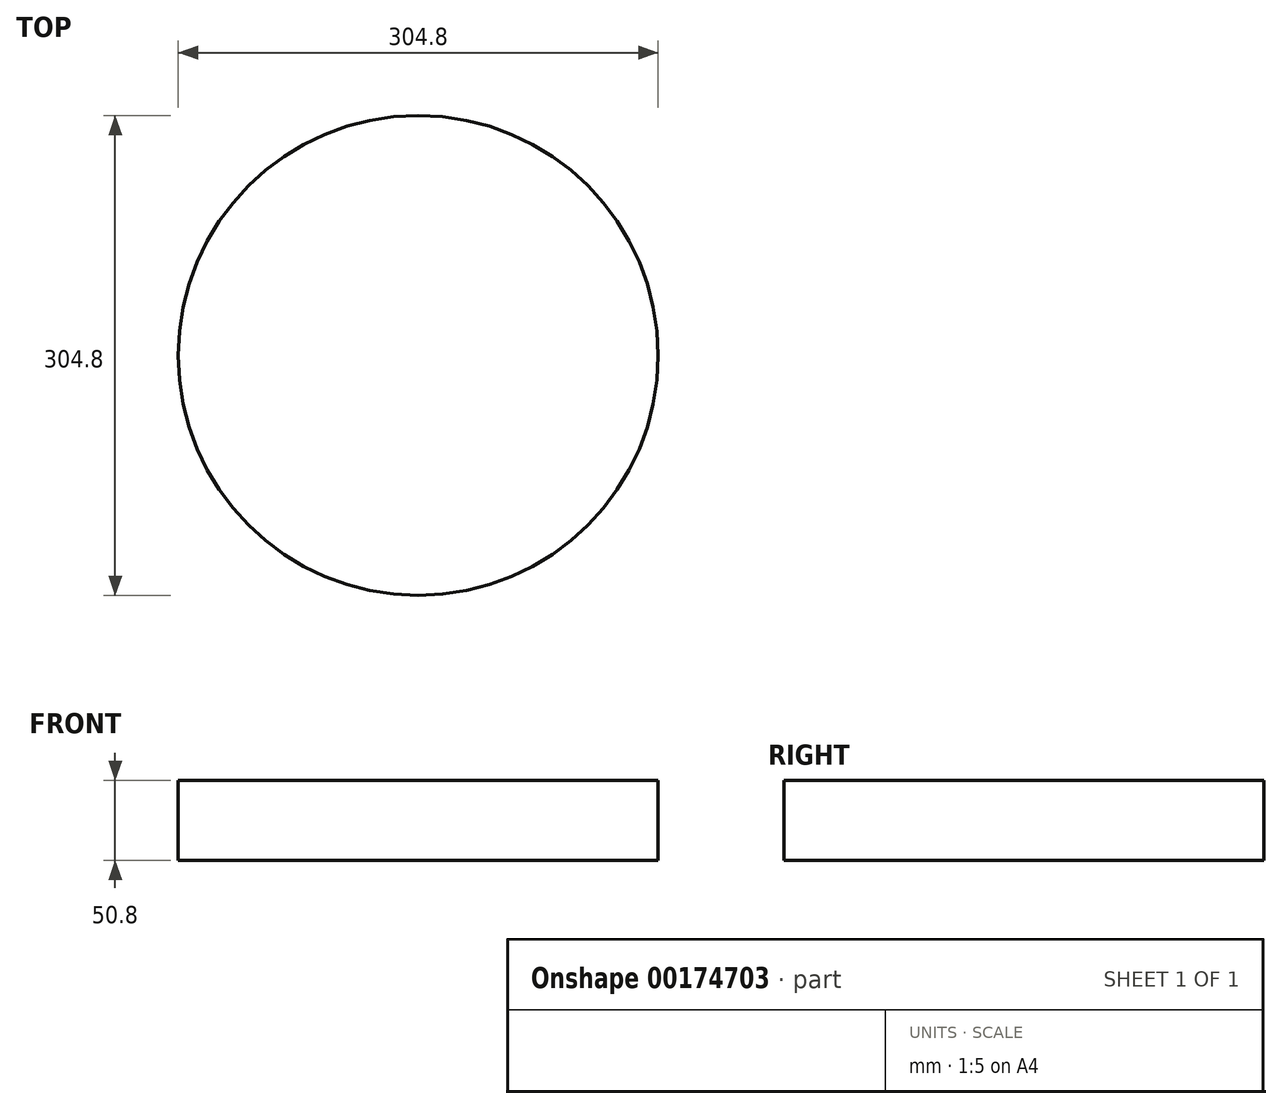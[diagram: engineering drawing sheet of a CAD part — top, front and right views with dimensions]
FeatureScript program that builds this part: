
annotation { "Feature Type Name" : "Feature", "Feature Type Description" : "" }
export const myFeature = defineFeature(function(context is Context, id is Id, definition is map)
    precondition{}
    {
        {
            var Q0;
            Q0=qCreatedBy(makeId("Top.planeOp"),FACE);
            var sketch = newSketch(context, id + "F0", { "sketchPlane" : qUnion([Q0])});
            skCircle(sketch, "E0", {"center": v(0, 0) * mm, "radius": 152.4 * mm});
            skSolve(sketch);
        }
        {
            var Q0;
            Q0 = qSketchRegion(id + "F0", true);
            extrude(context, id + "F1", {"entities" : qUnion([Q0]), "depth" : 50.8 * mm});
        }
    });
